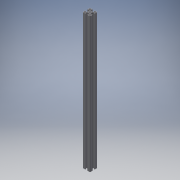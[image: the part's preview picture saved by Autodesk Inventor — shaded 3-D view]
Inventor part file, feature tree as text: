
AUTODESK INVENTOR PART (.ipt)
format: ipt  version: 2019 (Build 230136000, 136)  size: 144,896 bytes
history: native  units: mm
features: other x1, extrude x1, sketch x1
ambient origin geometry x8: Origin, YZ Plane, XZ Plane, XY Plane, X Axis, Y Axis, Z Axis, Center Point
bodies: Body1 (feature_tree)
feature tree (3):
  other  "솔리드1"
  extrude  "돌출1"  Depth=370.0mm TaperAngle=0.0deg
  sketch  "스케치1"
